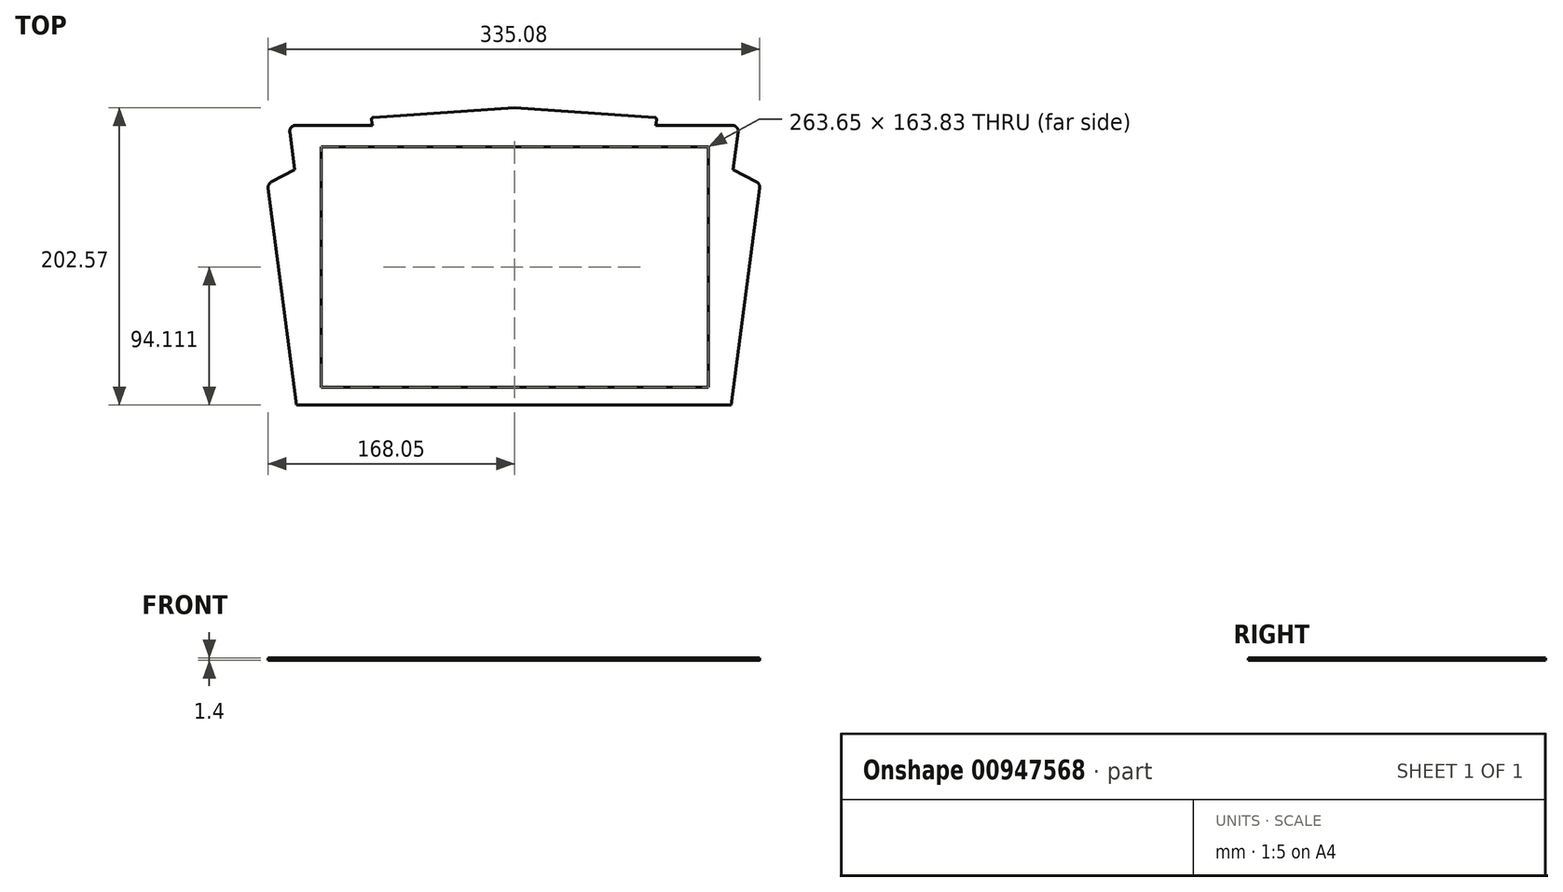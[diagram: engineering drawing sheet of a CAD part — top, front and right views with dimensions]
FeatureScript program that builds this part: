
annotation { "Feature Type Name" : "Feature", "Feature Type Description" : "" }
export const myFeature = defineFeature(function(context is Context, id is Id, definition is map)
    precondition{}
    {
        {
            var Q0;
            Q0=qCreatedBy(makeId("Top.planeOp"),FACE);
            var sketch = newSketch(context, id + "F0", { "sketchPlane" : qUnion([Q0])});
            skLineSegment(sketch, "E0", {"start": v(-131.83, 124.8) * mm, "end": v(-131.83, -39.03) * mm});
            skLineSegment(sketch, "E1", {"start": v(-131.83, 124.8) * mm, "end": v(0, 124.8) * mm});
            skLineSegment(sketch, "E2", {"start": v(-131.83, -39.03) * mm, "end": v(-1.02, -39.03) * mm});
            skLineSegment(sketch, "E3.MirrorCS", {"start": v(130.8, 124.8) * mm, "end": v(0, 124.8) * mm});
            skLineSegment(sketch, "E4.MirrorCS", {"start": v(131.83, 124.8) * mm, "end": v(131.83, -39.03) * mm});
            skLineSegment(sketch, "E5.MirrorCS", {"start": v(131.83, -39.03) * mm, "end": v(-1.02, -39.03) * mm});
            skLineSegment(sketch, "E6", {"start": v(-153.91, 139.4) * mm, "end": v(-97.1, 139.4) * mm});
            skLineSegment(sketch, "E7", {"start": v(-148.56, -51.23) * mm, "end": v(0, -51.23) * mm});
            skLineSegment(sketch, "E8", {"start": v(-148.56, -51.23) * mm, "end": v(-168.4, 99.44) * mm});
            skLineSegment(sketch, "E9", {"start": v(-168.4, 99.44) * mm, "end": v(-149.92, 109.06) * mm});
            skLineSegment(sketch, "E10", {"start": v(-149.92, 109.06) * mm, "end": v(-153.91, 139.4) * mm});
            skLineSegment(sketch, "E11", {"start": v(-97.1, 139.4) * mm, "end": v(-97.9, 144.54) * mm});
            skLineSegment(sketch, "E12", {"start": v(-26.05, 151.34) * mm, "end": v(43.88, 151.34) * mm, "construction": true});
            skLineSegment(sketch, "E13", {"start": v(-97.9, 144.54) * mm, "end": v(0, 151.34) * mm});
            skLineSegment(sketch, "E14.MirrorCS", {"start": v(96.9, 144.63) * mm, "end": v(0, 151.34) * mm});
            skLineSegment(sketch, "E15.MirrorCS", {"start": v(96.08, 139.4) * mm, "end": v(96.9, 144.63) * mm});
            skLineSegment(sketch, "E16.MirrorCS", {"start": v(152.9, 139.4) * mm, "end": v(96.08, 139.4) * mm});
            skLineSegment(sketch, "E17.MirrorCS", {"start": v(148.9, 109.06) * mm, "end": v(152.9, 139.4) * mm});
            skLineSegment(sketch, "E18.MirrorCS", {"start": v(167.38, 99.44) * mm, "end": v(148.9, 109.06) * mm});
            skLineSegment(sketch, "E19.MirrorCS", {"start": v(147.54, -51.23) * mm, "end": v(167.38, 99.44) * mm});
            skLineSegment(sketch, "E20.MirrorCS", {"start": v(147.54, -51.23) * mm, "end": v(0, -51.23) * mm});
            skLineSegment(sketch, "E21", {"start": v(0, 0) * mm, "end": v(0, 177.73) * mm, "construction": true});
            skLineSegment(sketch, "E22", {"start": v(130.8, 124.8) * mm, "end": v(131.83, 124.8) * mm});
            skSolve(sketch);
        }
        {
            var Q0;
            Q0=makeQuery(id+"F0.imprint","IMPRINT",FACE,{"disambiguationData":[TD([[makeQuery(id+"F0.imprint","IMPRINT",EDGE,{"derivedFrom":sQuery(id+"F0.wireOp",EDGE,"E0")}),-1.0]])]});
            extrude(context, id + "F1", {"entities" : qUnion([Q0]), "depth" : 1.4 * mm, "offsetDistance" : 25.4 * mm});
        }
        {
            var Q0;
            Q0=makeQuery(id+"F1.opExtrude","SWEPT_EDGE",EDGE,{"disambiguationData":[OSD([sQuery(id+"F0.wireOp",EDGE,"E6"),sQuery(id+"F0.wireOp",EDGE,"E10")])]});
            var Q1;
            Q1=makeQuery(id+"F1.opExtrude","SWEPT_EDGE",EDGE,{"disambiguationData":[OSD([sQuery(id+"F0.wireOp",EDGE,"E16.MirrorCS"),sQuery(id+"F0.wireOp",EDGE,"E17.MirrorCS")])]});
            var Q2;
            Q2=makeQuery(id+"F1.opExtrude","SWEPT_EDGE",EDGE,{"disambiguationData":[OSD([sQuery(id+"F0.wireOp",EDGE,"E8"),sQuery(id+"F0.wireOp",EDGE,"E9")])]});
            var Q3;
            Q3=makeQuery(id+"F1.opExtrude","SWEPT_EDGE",EDGE,{"disambiguationData":[OSD([sQuery(id+"F0.wireOp",EDGE,"E18.MirrorCS"),sQuery(id+"F0.wireOp",EDGE,"E19.MirrorCS")])]});
            fillet(context, id + "F2", {"entities" : qUnion([Q0, Q1, Q2, Q3]), "radius" : 4.14 * mm, "tangentPropagation" : true, "allowEdgeOverflow" : false});
        }
        {
            var Q0;
            Q0=makeQuery(id+"F1.opExtrude","SWEPT_EDGE",EDGE,{"disambiguationData":[OSD([sQuery(id+"F0.wireOp",EDGE,"E14.MirrorCS"),sQuery(id+"F0.wireOp",EDGE,"E15.MirrorCS")])]});
            var Q1;
            Q1=makeQuery(id+"F1.opExtrude","SWEPT_EDGE",EDGE,{"disambiguationData":[OSD([sQuery(id+"F0.wireOp",EDGE,"E11"),sQuery(id+"F0.wireOp",EDGE,"E13")])]});
            fillet(context, id + "F3", {"entities" : qUnion([Q0, Q1]), "radius" : 1.4 * mm, "tangentPropagation" : true, "allowEdgeOverflow" : false});
        }
    });
